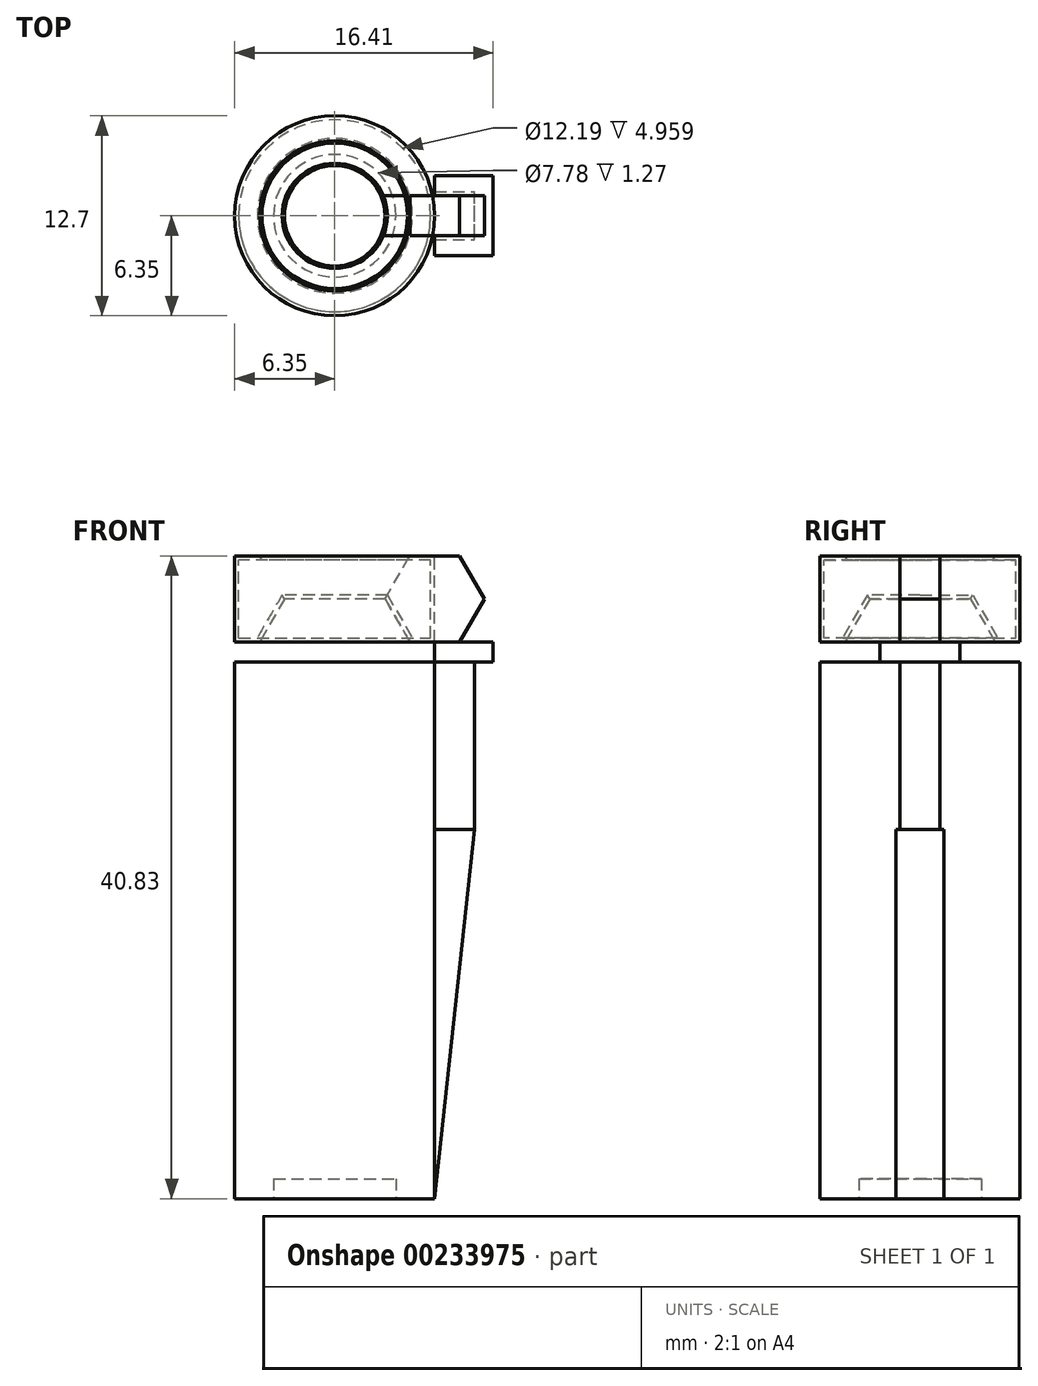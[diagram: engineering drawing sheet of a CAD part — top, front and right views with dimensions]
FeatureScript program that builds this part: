
annotation { "Feature Type Name" : "Feature", "Feature Type Description" : "" }
export const myFeature = defineFeature(function(context is Context, id is Id, definition is map)
    precondition{}
    {
        {
            var Q0;
            Q0=qCreatedBy(makeId("Front.planeOp"),FACE);
            var sketch = newSketch(context, id + "F0", { "sketchPlane" : qUnion([Q0])});
            skLineSegment(sketch, "E0.bottom", {"start": v(6.35, -19.05) * mm, "end": v(-6.35, -19.05) * mm});
            skLineSegment(sketch, "E0.top", {"start": v(6.35, 19.05) * mm, "end": v(-6.35, 19.05) * mm});
            skLineSegment(sketch, "E0.left", {"start": v(6.35, -19.05) * mm, "end": v(6.35, 19.05) * mm});
            skLineSegment(sketch, "E0.right", {"start": v(-6.35, -19.05) * mm, "end": v(-6.35, 19.05) * mm});
            skPoint(sketch, "E0.middle", {"position": v(0, 0) * mm});
            skLineSegment(sketch, "E1", {"start": v(6.35, -19.05) * mm, "end": v(8.9, 4.4) * mm});
            skLineSegment(sketch, "E2", {"start": v(8.9, 4.4) * mm, "end": v(6.35, 4.4) * mm});
            skLineSegment(sketch, "E3", {"start": v(8.9, 4.4) * mm, "end": v(8.9, 15.05) * mm});
            skLineSegment(sketch, "E4", {"start": v(8.9, 15.05) * mm, "end": v(10.06, 15.05) * mm});
            skLineSegment(sketch, "E5", {"start": v(10.06, 15.05) * mm, "end": v(10.06, 15.05) * mm});
            skLineSegment(sketch, "E6", {"start": v(10.06, 15.05) * mm, "end": v(10.06, 16.32) * mm});
            skLineSegment(sketch, "E7", {"start": v(10.06, 16.32) * mm, "end": v(6.35, 16.32) * mm});
            skLineSegment(sketch, "E8.bottom", {"start": v(6.35, 15.05) * mm, "end": v(-6.35, 15.05) * mm});
            skLineSegment(sketch, "E8.top", {"start": v(6.35, 23.05) * mm, "end": v(-6.35, 23.05) * mm});
            skLineSegment(sketch, "E8.left", {"start": v(6.35, 15.05) * mm, "end": v(6.35, 23.05) * mm});
            skLineSegment(sketch, "E8.right", {"start": v(-6.35, 15.05) * mm, "end": v(-6.35, 23.05) * mm});
            skPoint(sketch, "E8.middle", {"position": v(0, 19.05) * mm});
            skLineSegment(sketch, "E9", {"start": v(0, 29.12) * mm, "end": v(0, -26.28) * mm});
            skPoint(sketch, "E9.startSnap0", {"position": v(0, 23.05) * mm});
            skPoint(sketch, "E9.endSnap0", {"position": v(0, -19.05) * mm});
            skLineSegment(sketch, "E10", {"start": v(8.9, 15.05) * mm, "end": v(6.35, 15.05) * mm});
            skCircle(sketch, "E11.cCircle", {"center": v(6.35, 19.05) * mm, "radius": 2.73 * mm, "construction": true});
            skLineSegment(sketch, "E11.0", {"start": v(7.93, 16.32) * mm, "end": v(4.77, 16.32) * mm});
            skLineSegment(sketch, "E11.1", {"start": v(4.77, 16.32) * mm, "end": v(3.2, 19.05) * mm});
            skLineSegment(sketch, "E11.2", {"start": v(3.2, 19.05) * mm, "end": v(4.77, 21.78) * mm});
            skLineSegment(sketch, "E11.3", {"start": v(4.77, 21.78) * mm, "end": v(7.93, 21.78) * mm});
            skLineSegment(sketch, "E11.4", {"start": v(7.93, 21.78) * mm, "end": v(9.5, 19.05) * mm});
            skLineSegment(sketch, "E11.5", {"start": v(9.5, 19.05) * mm, "end": v(7.93, 16.32) * mm});
            skPoint(sketch, "E11.0.midPoint", {"position": v(6.35, 16.32) * mm});
            skSolve(sketch);
        }
        {
            var Q0;
            {var subQ3=sQuery(id+"F0.wireOp",EDGE,"E9");var subQ5=sQuery(id+"F0.wireOp",EDGE,"E0.bottom");var subQ6=makeQuery(id+"F0.imprint","INTERSECT",VERTEX,{"derivedFrom":[subQ5,subQ3]});Q0=makeQuery(id+"F0.imprint","IMPRINT",FACE,{"disambiguationData":[TD([[makeQuery(id+"F0.imprint","IMPRINT",EDGE,{"disambiguationData":[TD([[subQ6,1.0]])],"derivedFrom":subQ3}),1.0]])]});}
            var Q1;
            Q1=sQuery(id+"F0.wireOp",EDGE,"E9");
            revolve(context, id + "F1", {"entities" : qUnion([Q0]), "axis" : qUnion([Q1]), "revolveType" : RevolveType.FULL});
        }
        {
            var Q0;
            {var subQ0=sQuery(id+"F0.wireOp",EDGE,"E8.left");var subQ6=sQuery(id+"F0.wireOp",EDGE,"E0.top");var subQ7=makeQuery(id+"F0.imprint","INTERSECT",VERTEX,{"derivedFrom":[subQ6,subQ0]});Q0=makeQuery(id+"F0.imprint","IMPRINT",FACE,{"disambiguationData":[TD([[makeQuery(id+"F0.imprint","IMPRINT",EDGE,{"disambiguationData":[TD([[subQ7,-1.0]])],"derivedFrom":subQ6}),1.0]])]});}
            var Q1;
            {var subQ0=sQuery(id+"F0.wireOp",EDGE,"E8.left");var subQ1=sQuery(id+"F0.wireOp",EDGE,"E0.top");var subQ2=makeQuery(id+"F0.imprint","INTERSECT",VERTEX,{"derivedFrom":[subQ1,subQ0]});Q1=makeQuery(id+"F0.imprint","IMPRINT",FACE,{"disambiguationData":[TD([[makeQuery(id+"F0.imprint","IMPRINT",EDGE,{"disambiguationData":[TD([[subQ2,-1.0]])],"derivedFrom":subQ1}),-1.0]])]});}
            var Q2;
            Q2=sQuery(id+"F0.wireOp",EDGE,"E9");
            revolve(context, id + "F2", {"entities" : qUnion([Q0, Q1]), "axis" : qUnion([Q2]), "revolveType" : RevolveType.FULL});
        }
        {
            var Q0;
            {var subQ0=sQuery(id+"F0.wireOp",EDGE,"E1");Q0=makeQuery(id+"F0.imprint","IMPRINT",FACE,{"disambiguationData":[TD([[makeQuery(id+"F0.imprint","IMPRINT",EDGE,{"derivedFrom":subQ0}),1.0]])]});}
            extrude(context, id + "F3", {"entities" : qUnion([Q0]), "endBound" : BoundingType.SYMMETRIC, "depth" : 3.05 * mm});
        }
        {
            var Q0;
            {var subQ0=sQuery(id+"F0.wireOp",EDGE,"E2");Q0=makeQuery(id+"F0.imprint","IMPRINT",FACE,{"disambiguationData":[TD([[makeQuery(id+"F0.imprint","IMPRINT",EDGE,{"derivedFrom":subQ0}),-1.0]])]});}
            extrude(context, id + "F4", {"entities" : qUnion([Q0]), "endBound" : BoundingType.SYMMETRIC, "depth" : 2.54 * mm});
        }
        {
            var Q0;
            Q0=makeQuery(id+"F0.imprint","IMPRINT",FACE,{"disambiguationData":[TD([[makeQuery(id+"F0.imprint","IMPRINT",EDGE,{"derivedFrom":sQuery(id+"F0.wireOp",EDGE,"E4")}),1.0]])]});
            extrude(context, id + "F7", {"entities" : qUnion([Q0]), "endBound" : BoundingType.SYMMETRIC, "depth" : 5.08 * mm});
        }
        {
            var Q0;
            {var subQ0=sQuery(id+"F0.wireOp",EDGE,"E11.4");Q0=makeQuery(id+"F0.imprint","IMPRINT",FACE,{"disambiguationData":[TD([[makeQuery(id+"F0.imprint","IMPRINT",EDGE,{"derivedFrom":subQ0}),-1.0]])]});}
            var Q1;
            {var subQ3=sQuery(id+"F0.wireOp",EDGE,"E11.2");Q1=makeQuery(id+"F0.imprint","IMPRINT",FACE,{"disambiguationData":[TD([[makeQuery(id+"F0.imprint","IMPRINT",EDGE,{"derivedFrom":subQ3}),-1.0]])]});}
            var Q2;
            {var subQ3=sQuery(id+"F0.wireOp",EDGE,"E11.1");Q2=makeQuery(id+"F0.imprint","IMPRINT",FACE,{"disambiguationData":[TD([[makeQuery(id+"F0.imprint","IMPRINT",EDGE,{"derivedFrom":subQ3}),-1.0]])]});}
            extrude(context, id + "F5", {"entities" : qUnion([Q0, Q1, Q2]), "endBound" : BoundingType.SYMMETRIC, "depth" : 2.54 * mm});
        }
        {
            var Q0;
            Q0=makeQuery(id+"F2.opRevolve","SWEPT_FACE",FACE,{"disambiguationData":[OSD([sQuery(id+"F0.wireOp",EDGE,"E11.2")])]});
            shell(context, id + "F6", {"entities" : qUnion([Q0]), "thickness" : 0.25 * mm});
        }
        {
            var Q0;
            Q0=makeQuery(id+"F1.opRevolve","SWEPT_FACE",FACE,{"disambiguationData":[OSD([sQuery(id+"F0.wireOp",EDGE,"E0.bottom")])]});
            var sketch = newSketch(context, id + "F8", { "sketchPlane" : qUnion([Q0])});
            skCircle(sketch, "E12", {"center": v(0, 0) * mm, "radius": 3.89 * mm});
            skSolve(sketch);
        }
        {
            var Q0;
            Q0 = qSketchRegion(id + "F8", true);
            extrude(context, id + "F9", {"entities" : qUnion([Q0]), "operationType" : NewBodyOperationType.REMOVE, "oppositeDirection" : true, "depth" : 1.27 * mm});
        }
    });
